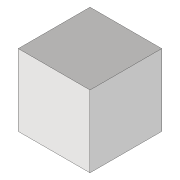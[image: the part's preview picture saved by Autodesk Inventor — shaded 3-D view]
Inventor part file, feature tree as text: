
AUTODESK INVENTOR PART (.ipt)
format: ipt  version: 2020 (Build 240168000, 168)  size: 74,240 bytes
history: native  units: mm
features: sketch x1, extrude x1
ambient origin geometry x8: Origin, YZ Plane, XZ Plane, XY Plane, X Axis, Y Axis, Z Axis, Center Point
bodies: Volumenkörper1 (feature_tree)
feature tree (2):
  sketch  "Skizze1"  dims[d0=1.0mm d1=1.0mm d3=0.0mm d4=1.0mm]
  extrude  "Extrusion1"  [1 undecoded]
note: 1 required parameter value undecoded (feature->parameter linkage not recoverable at this tier; creation-order binding heuristic only, values carry confidence <= 0.55)
